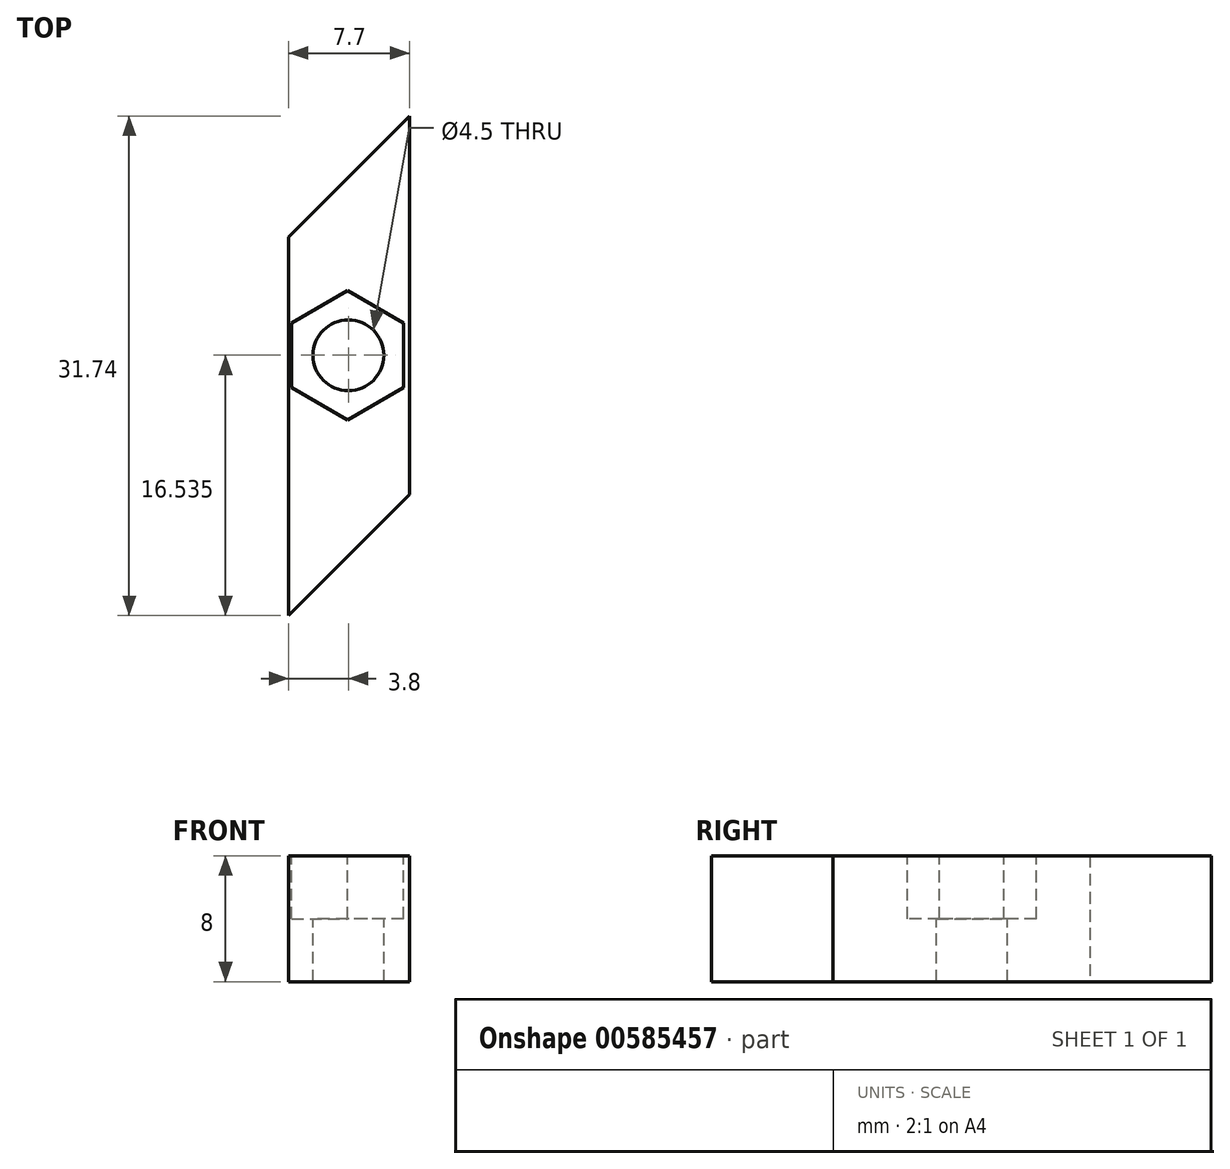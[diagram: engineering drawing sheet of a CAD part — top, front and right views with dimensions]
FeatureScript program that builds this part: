
annotation { "Feature Type Name" : "Feature", "Feature Type Description" : "" }
export const myFeature = defineFeature(function(context is Context, id is Id, definition is map)
    precondition{}
    {
        {
            var Q0;
            Q0=qCreatedBy(makeId("Top.planeOp"),FACE);
            var sketch = newSketch(context, id + "F0", { "sketchPlane" : qUnion([Q0])});
            skLineSegment(sketch, "E0", {"start": v(0, 0) * mm, "end": v(7.7, 7.7) * mm});
            skLineSegment(sketch, "E1", {"start": v(7.7, 7.7) * mm, "end": v(7.7, 31.74) * mm});
            skLineSegment(sketch, "E2", {"start": v(7.7, 31.74) * mm, "end": v(0, 24.04) * mm});
            skLineSegment(sketch, "E3", {"start": v(0, 24.04) * mm, "end": v(0, 0) * mm});
            skSolve(sketch);
        }
        {
            var Q0;
            Q0=makeQuery(id+"F0.imprint","IMPRINT",FACE,{"disambiguationData":[TD([[makeQuery(id+"F0.imprint","IMPRINT",EDGE,{"derivedFrom":sQuery(id+"F0.wireOp",EDGE,"E0")}),1.0]])]});
            extrude(context, id + "F1", {"entities" : qUnion([Q0]), "depth" : 8 * mm, "offsetDistance" : 25 * mm});
        }
        {
            var Q0;
            Q0=makeQuery(id+"F1.opExtrude","CAP_FACE",FACE,{"disambiguationData":[OSD([sQuery(id+"F0.wireOp",EDGE,"E0"),sQuery(id+"F0.wireOp",EDGE,"E1"),sQuery(id+"F0.wireOp",EDGE,"E2"),sQuery(id+"F0.wireOp",EDGE,"E3")])],"isStart":false});
            var sketch = newSketch(context, id + "F2", { "sketchPlane" : qUnion([Q0])});
            skCircle(sketch, "E4.cCircle", {"center": v(3.75, 16.53) * mm, "radius": 3.55 * mm, "construction": true});
            skLineSegment(sketch, "E4.0", {"start": v(7.3, 14.49) * mm, "end": v(3.75, 12.44) * mm});
            skLineSegment(sketch, "E4.1", {"start": v(3.75, 12.44) * mm, "end": v(0.2, 14.49) * mm});
            skLineSegment(sketch, "E4.2", {"start": v(0.2, 14.49) * mm, "end": v(0.2, 18.58) * mm});
            skLineSegment(sketch, "E4.3", {"start": v(0.2, 18.58) * mm, "end": v(3.75, 20.63) * mm});
            skLineSegment(sketch, "E4.4", {"start": v(3.75, 20.63) * mm, "end": v(7.3, 18.58) * mm});
            skLineSegment(sketch, "E4.5", {"start": v(7.3, 18.58) * mm, "end": v(7.3, 14.49) * mm});
            skPoint(sketch, "E4.0.midPoint", {"position": v(5.52, 13.46) * mm});
            skSolve(sketch);
        }
        {
            var Q0;
            Q0 = qSketchRegion(id + "F2", true);
            extrude(context, id + "F3", {"entities" : qUnion([Q0]), "operationType" : NewBodyOperationType.REMOVE, "oppositeDirection" : true, "depth" : 4 * mm, "offsetDistance" : 25 * mm});
        }
        {
            var Q0;
            Q0=makeQuery(id+"F3.boolean.opBoolean","COPY",FACE,{"derivedFrom":makeQuery(id+"F3.opExtrude","CAP_FACE",FACE,{"disambiguationData":[OSD([sQuery(id+"F2.wireOp",EDGE,"E4.0"),sQuery(id+"F2.wireOp",EDGE,"E4.1"),sQuery(id+"F2.wireOp",EDGE,"E4.2"),sQuery(id+"F2.wireOp",EDGE,"E4.3"),sQuery(id+"F2.wireOp",EDGE,"E4.4"),sQuery(id+"F2.wireOp",EDGE,"E4.5")])],"isStart":false})});
            var sketch = newSketch(context, id + "F4", { "sketchPlane" : qUnion([Q0])});
            skCircle(sketch, "E5", {"center": v(3.8, 16.53) * mm, "radius": 2.25 * mm});
            skPoint(sketch, "E5.centerSnap0", {"position": v(7.3, 16.53) * mm});
            skSolve(sketch);
        }
        {
            var Q0;
            Q0 = qSketchRegion(id + "F4", true);
            extrude(context, id + "F5", {"entities" : qUnion([Q0]), "operationType" : NewBodyOperationType.REMOVE, "oppositeDirection" : true, "depth" : 25 * mm, "offsetDistance" : 25 * mm});
        }
    });
